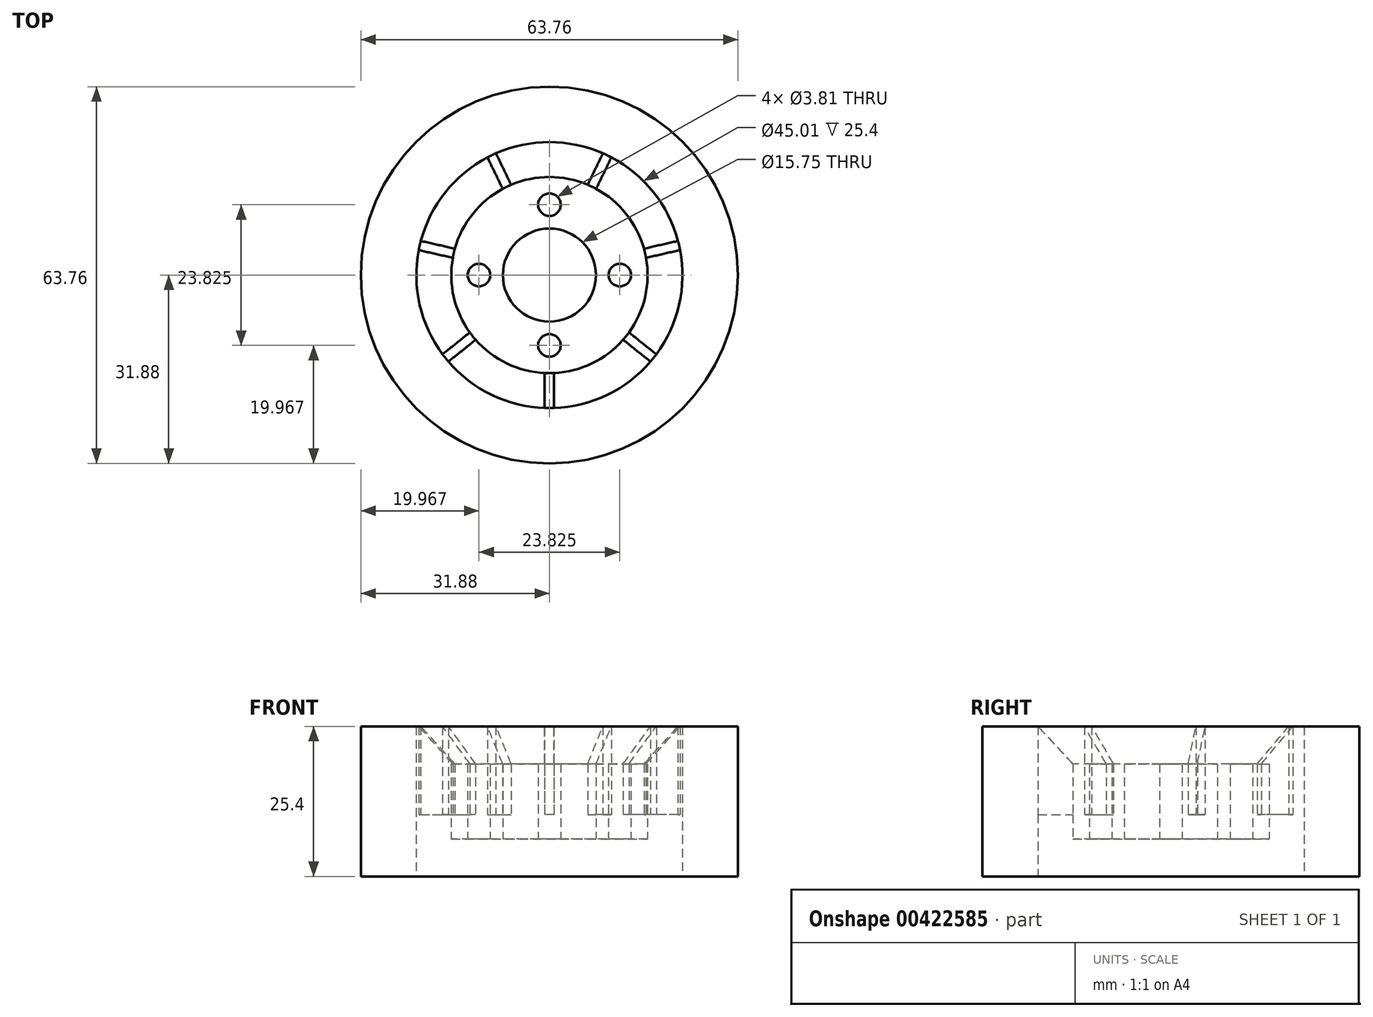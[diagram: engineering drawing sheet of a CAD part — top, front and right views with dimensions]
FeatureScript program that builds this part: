
annotation { "Feature Type Name" : "Feature", "Feature Type Description" : "" }
export const myFeature = defineFeature(function(context is Context, id is Id, definition is map)
    precondition{}
    {
        {
            var Q0;
            Q0=qCreatedBy(makeId("Top.planeOp"),FACE);
            var sketch = newSketch(context, id + "F0", { "sketchPlane" : qUnion([Q0])});
            skCircle(sketch, "E0", {"center": v(0, 0) * mm, "radius": 7.87 * mm});
            skCircle(sketch, "E1", {"center": v(0, 0) * mm, "radius": 31.88 * mm});
            skCircle(sketch, "E2", {"center": v(0, 0) * mm, "radius": 16.6 * mm});
            skCircle(sketch, "E3", {"center": v(0, 0) * mm, "radius": 11.91 * mm, "construction": true});
            skLineSegment(sketch, "E4", {"start": v(0, 14.14) * mm, "end": v(0, -13.44) * mm, "construction": true});
            skLineSegment(sketch, "E5", {"start": v(-14.4, 0) * mm, "end": v(14.7, 0) * mm, "construction": true});
            skCircle(sketch, "E6", {"center": v(0, 11.91) * mm, "radius": 1.9 * mm});
            skCircle(sketch, "E7", {"center": v(-11.91, 0) * mm, "radius": 1.9 * mm});
            skCircle(sketch, "E8", {"center": v(0, -11.91) * mm, "radius": 1.9 * mm});
            skCircle(sketch, "E9", {"center": v(11.91, 0) * mm, "radius": 1.9 * mm});
            skCircle(sketch, "E10", {"center": v(0, 0) * mm, "radius": 22.5 * mm});
            skSolve(sketch);
        }
        {
            var Q0;
            Q0=makeQuery(id+"F0.imprint","IMPRINT",FACE,{"disambiguationData":[TD([[makeQuery(id+"F0.imprint","IMPRINT",EDGE,{"derivedFrom":sQuery(id+"F0.wireOp",EDGE,"E1")}),1.0]])]});
            extrude(context, id + "F1", {"entities" : qUnion([Q0]), "endBound" : BoundingType.SYMMETRIC, "depth" : 25.4 * mm});
        }
        {
            var Q0;
            Q0=makeQuery(id+"F0.imprint","IMPRINT",FACE,{"disambiguationData":[TD([[makeQuery(id+"F0.imprint","IMPRINT",EDGE,{"derivedFrom":sQuery(id+"F0.wireOp",EDGE,"E0")}),-1.0]])]});
            extrude(context, id + "F2", {"entities" : qUnion([Q0]), "endBound" : BoundingType.SYMMETRIC, "depth" : 12.7 * mm});
        }
        {
            var Q0;
            Q0=makeQuery(id+"F2.opExtrude","CAP_FACE",FACE,{"disambiguationData":[OSD([sQuery(id+"F0.wireOp",EDGE,"E0"),sQuery(id+"F0.wireOp",EDGE,"E2"),sQuery(id+"F0.wireOp",EDGE,"E6"),sQuery(id+"F0.wireOp",EDGE,"E7"),sQuery(id+"F0.wireOp",EDGE,"E8"),sQuery(id+"F0.wireOp",EDGE,"E9")])],"isStart":true});
            cPlane(context, id + "F3", {"entities" : qUnion([Q0]), "cplaneType" : CPlaneType.OFFSET, "offset" : 4.13 * mm, "oppositeDirection" : true, "width" : 152.4 * mm, "height" : 152.4 * mm});
        }
        {
            var Q0;
            Q0=qCreatedBy(id+"F3.planeOp",FACE);
            var sketch = newSketch(context, id + "F4", { "sketchPlane" : qUnion([Q0])});
            skCircle(sketch, "E11.0.0", {"center": v(0, 0) * mm, "radius": 16.6 * mm});
            skCircle(sketch, "E12.0.0", {"center": v(0, 0) * mm, "radius": 31.88 * mm});
            skLineSegment(sketch, "E13", {"start": v(0, 0) * mm, "end": v(0, 22.44) * mm, "construction": true});
            skCircle(sketch, "E14.0", {"center": v(0, 0) * mm, "radius": 22.5 * mm});
            skLineSegment(sketch, "E15", {"start": v(-0.8, 22.5) * mm, "end": v(-0.8, 16.58) * mm});
            skLineSegment(sketch, "E16", {"start": v(0.8, 22.5) * mm, "end": v(0.8, 16.58) * mm});
            skLineSegment(sketch, "E17.1.1", {"start": v(-18.08, 13.4) * mm, "end": v(-13.46, 9.72) * mm});
            skLineSegment(sketch, "E17.1.2", {"start": v(-17.09, 14.64) * mm, "end": v(-12.47, 10.96) * mm});
            skLineSegment(sketch, "E17.2.1", {"start": v(-21.75, -5.78) * mm, "end": v(-15.99, -4.46) * mm});
            skLineSegment(sketch, "E17.2.2", {"start": v(-22.1, -4.23) * mm, "end": v(-16.34, -2.92) * mm});
            skLineSegment(sketch, "E17.3.1", {"start": v(-9.04, -20.6) * mm, "end": v(-6.48, -15.28) * mm});
            skLineSegment(sketch, "E17.3.2", {"start": v(-10.47, -19.92) * mm, "end": v(-7.9, -14.6) * mm});
            skLineSegment(sketch, "E17.4.1", {"start": v(10.47, -19.92) * mm, "end": v(7.9, -14.6) * mm});
            skLineSegment(sketch, "E17.4.2", {"start": v(9.04, -20.6) * mm, "end": v(6.48, -15.28) * mm});
            skLineSegment(sketch, "E17.5.1", {"start": v(22.1, -4.23) * mm, "end": v(16.34, -2.92) * mm});
            skLineSegment(sketch, "E17.5.2", {"start": v(21.75, -5.78) * mm, "end": v(15.99, -4.46) * mm});
            skLineSegment(sketch, "E17.6.1", {"start": v(17.09, 14.64) * mm, "end": v(12.47, 10.96) * mm});
            skLineSegment(sketch, "E17.6.2", {"start": v(18.08, 13.4) * mm, "end": v(13.46, 9.72) * mm});
            skSolve(sketch);
        }
        {
            var Q0;
            {var subQ0=sQuery(id+"F4.wireOp",EDGE,"E17.1.1");Q0=makeQuery(id+"F4.imprint","IMPRINT",FACE,{"disambiguationData":[TD([[makeQuery(id+"F4.imprint","IMPRINT",EDGE,{"derivedFrom":subQ0}),1.0]])]});}
            var Q1;
            {var subQ0=sQuery(id+"F4.wireOp",EDGE,"E15");Q1=makeQuery(id+"F4.imprint","IMPRINT",FACE,{"disambiguationData":[TD([[makeQuery(id+"F4.imprint","IMPRINT",EDGE,{"derivedFrom":subQ0}),1.0]])]});}
            var Q2;
            {var subQ0=sQuery(id+"F4.wireOp",EDGE,"E17.6.1");Q2=makeQuery(id+"F4.imprint","IMPRINT",FACE,{"disambiguationData":[TD([[makeQuery(id+"F4.imprint","IMPRINT",EDGE,{"derivedFrom":subQ0}),1.0]])]});}
            var Q3;
            {var subQ0=sQuery(id+"F4.wireOp",EDGE,"E17.5.1");Q3=makeQuery(id+"F4.imprint","IMPRINT",FACE,{"disambiguationData":[TD([[makeQuery(id+"F4.imprint","IMPRINT",EDGE,{"derivedFrom":subQ0}),1.0]])]});}
            var Q4;
            {var subQ0=sQuery(id+"F4.wireOp",EDGE,"E17.4.1");Q4=makeQuery(id+"F4.imprint","IMPRINT",FACE,{"disambiguationData":[TD([[makeQuery(id+"F4.imprint","IMPRINT",EDGE,{"derivedFrom":subQ0}),1.0]])]});}
            var Q5;
            {var subQ0=sQuery(id+"F4.wireOp",EDGE,"E17.3.1");Q5=makeQuery(id+"F4.imprint","IMPRINT",FACE,{"disambiguationData":[TD([[makeQuery(id+"F4.imprint","IMPRINT",EDGE,{"derivedFrom":subQ0}),1.0]])]});}
            var Q6;
            {var subQ0=sQuery(id+"F4.wireOp",EDGE,"E17.2.1");Q6=makeQuery(id+"F4.imprint","IMPRINT",FACE,{"disambiguationData":[TD([[makeQuery(id+"F4.imprint","IMPRINT",EDGE,{"derivedFrom":subQ0}),1.0]])]});}
            var Q7;
            Q7=makeQuery(id+"F1.opExtrude","CAP_FACE",FACE,{"disambiguationData":[OSD([sQuery(id+"F0.wireOp",EDGE,"E1"),sQuery(id+"F0.wireOp",EDGE,"E10")])],"isStart":false});
            extrude(context, id + "F5", {"entities" : qUnion([Q0, Q1, Q2, Q3, Q4, Q5, Q6]), "operationType" : NewBodyOperationType.ADD, "endBound" : BoundingType.UP_TO_SURFACE, "oppositeDirection" : true, "endBoundEntityFace" : qUnion([Q7]), "depth" : 25.4 * mm});
        }
        {
            var Q0;
            Q0=makeQuery(id+"F5.opExtrude","SWEPT_FACE",FACE,{"disambiguationData":[OSD([sQuery(id+"F4.wireOp",EDGE,"E17.2.2")])]});
            var sketch = newSketch(context, id + "F6", { "sketchPlane" : qUnion([Q0])});
            skLineSegment(sketch, "E18", {"start": v(-22.5, 12.7) * mm, "end": v(-16.58, 6.35) * mm});
            skLineSegment(sketch, "E19", {"start": v(-16.58, 6.35) * mm, "end": v(-16.58, 12.7) * mm});
            skLineSegment(sketch, "E20", {"start": v(-16.58, 12.7) * mm, "end": v(-22.5, 12.7) * mm});
            skLineSegment(sketch, "E21.0", {"start": v(15.28, 6.35) * mm, "end": v(14.6, 6.35) * mm});
            skSolve(sketch);
        }
        {
            var Q0;
            Q0=qCreatedBy(makeId("Front.planeOp"),FACE);
            var sketch = newSketch(context, id + "F7", { "sketchPlane" : qUnion([Q0])});
            skLineSegment(sketch, "E22", {"start": v(0, 0) * mm, "end": v(0, 8.2) * mm, "construction": true});
            skSolve(sketch);
        }
        {
            var Q0;
            Q0=makeQuery(id+"F6.imprint","IMPRINT",FACE,{"disambiguationData":[TD([[makeQuery(id+"F6.imprint","IMPRINT",EDGE,{"derivedFrom":sQuery(id+"F6.wireOp",EDGE,"E18")}),1.0]])]});
            var Q1;
            Q1=sQuery(id+"F7.wireOp",EDGE,"E22");
            revolve(context, id + "F8", {"operationType" : NewBodyOperationType.REMOVE, "surfaceOperationType" : NewSurfaceOperationType.NEW, "entities" : qUnion([Q0]), "axis" : qUnion([Q1]), "revolveType" : RevolveType.ONE_DIRECTION, "oppositeDirection" : true, "angle" : 360 * degree});
        }
    });
